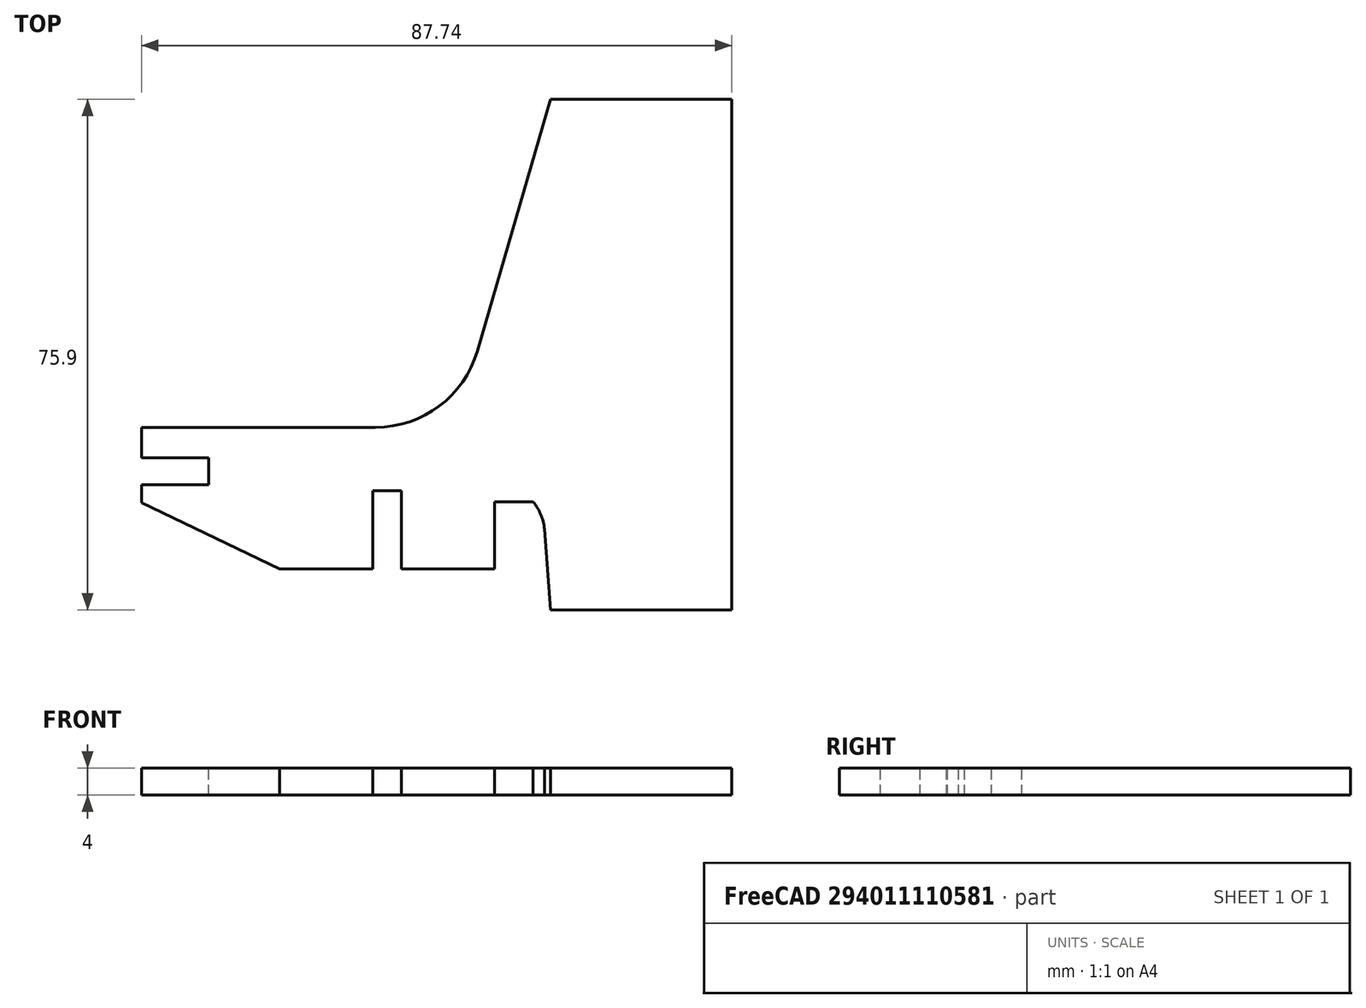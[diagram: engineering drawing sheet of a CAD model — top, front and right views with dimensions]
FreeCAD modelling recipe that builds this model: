
FCSTD DOCUMENT  (FreeCAD 0.18R16131 (Git))
Label: solo_banderuola4mm_v4
License: All rights reserved
LicenseURL: http://en.wikipedia.org/wiki/All_rights_reserved
objects: Sketcher::SketchObject×1, PartDesign::Pad×1, PartDesign::Body×1
note: 4 computed .brp shape members not serialized (recipe doc carries the construction recipe); baked Part::Feature solids carry a one-line shape summary decoded from their .brp

FEATURE [Sketcher::SketchObject] CopySketch004
  sketch-geometry (26):
    g0: LineSegment StartX=-36.5085 StartY=11.06 StartZ=0 EndX=-1.7237 EndY=11.06 EndZ=0
    g1: LineSegment StartX=13.4079 StartY=22.4098 StartZ=0 EndX=24.3191 EndY=59.8325 EndZ=0
    g2: LineSegment StartX=24.3191 StartY=59.8325 StartZ=0 EndX=51.2261 EndY=59.8325 EndZ=0
    g3: ArcOfCircle CenterX=-1.7237 CenterY=26.8216 CenterZ=0 NormalX=0 NormalY=0 NormalZ=1 AngleXU=0 Radius=15.7616 StartAngle=4.71239 EndAngle=5.99948
    g4: GeomPoint X=16 Y=0 Z=0
    g5: LineSegment StartX=-16 StartY=-10 StartZ=0 EndX=-2.15 EndY=-10 EndZ=0
    g6: LineSegment StartX=16 StartY=-10 StartZ=0 EndX=16 EndY=0 EndZ=0
    g7: GeomPoint X=-2.15 Y=-10 Z=0
    g8: GeomPoint X=2.15 Y=-10 Z=0
    g9: LineSegment StartX=-2.15 StartY=-10 StartZ=0 EndX=-2.15 EndY=1.64739 EndZ=0
    g10: LineSegment StartX=-2.15 StartY=1.64739 StartZ=0 EndX=2.15 EndY=1.64739 EndZ=0
    g11: LineSegment StartX=2.15 StartY=1.64739 StartZ=0 EndX=2.15 EndY=-10 EndZ=0
    g12: LineSegment StartX=2.15 StartY=-10 StartZ=0 EndX=16 EndY=-10 EndZ=0
    g13: ArcOfCircle CenterX=15.5785 CenterY=-4.94395 CenterZ=0 NormalX=0 NormalY=0 NormalZ=1 AngleXU=0 Radius=7.87288 StartAngle=0.112427 EndAngle=0.678944
    g14: LineSegment StartX=23.4017 StartY=-4.06069 StartZ=0 EndX=24.3191 EndY=-16.0675 EndZ=0
    g15: LineSegment StartX=24.3191 StartY=-16.0675 StartZ=0 EndX=51.2261 EndY=-16.0675 EndZ=0
    g16: LineSegment StartX=16 StartY=0 StartZ=0 EndX=21.7055 EndY=0 EndZ=0
    g17: LineSegment StartX=-36.5085 StartY=11.06 StartZ=0 EndX=-36.5085 EndY=6.54926 EndZ=0
    g18: LineSegment StartX=-16 StartY=-10 StartZ=0 EndX=-36.5085 EndY=-0.144815 EndZ=0
    g19: LineSegment StartX=-36.5085 StartY=6.54926 StartZ=0 EndX=-26.5085 EndY=6.54926 EndZ=0
    g20: LineSegment StartX=-26.5085 StartY=6.54926 StartZ=0 EndX=-26.5085 EndY=2.54926 EndZ=0
    g21: LineSegment StartX=-26.5085 StartY=2.54926 StartZ=0 EndX=-36.5085 EndY=2.54926 EndZ=0
    g22: LineSegment [constr] StartX=15.9818 StartY=5.77886 StartZ=0 EndX=-16.7629 EndY=5.77886 EndZ=0
    g23: LineSegment [constr] StartX=22.8928 StartY=7.91796 StartZ=0 EndX=-22.1107 EndY=7.91796 EndZ=0
    g24: LineSegment StartX=-36.5085 StartY=2.54926 StartZ=0 EndX=-36.5085 EndY=-0.144815 EndZ=0
    g25: LineSegment StartX=51.2261 StartY=59.8325 StartZ=0 EndX=51.2261 EndY=-16.0675 EndZ=0
  constraints (52):
    c: Horizontal(g0)
    c: Coincident(g1,g2)
    c: Horizontal(g2)
    c: Tangent(g0,g3) = -1.5708
    c: Tangent(g1,g3) = -1.5708
    c: Horizontal(g5)
    c: Coincident(g12,g6)
    c: Vertical(g6)
    c: Coincident(g6,g4)
    c: PointOnObject(g7,g5)
    c: DistanceY(g6,g6) = 10
    c: Symmetric(g7,g8,g-2)
    c: Coincident(g9,g7)
    c: Vertical(g9)
    c: Coincident(g9,g10)
    c: Horizontal(g10)
    c: Coincident(g10,g11)
    c: Coincident(g11,g8)
    c: Vertical(g11)
    c: PointOnObject(g5,g9)
    c: PointOnObject(g12,g11)
    c: Tangent(g5,g12)
    c: DistanceX(g5,g8) = 4.3
    c: Coincident(g14,g15)
    c: Horizontal(g15)
    c: PointOnObject(g4,g-1)
    c: Equal(g2,g15)
    c: Coincident(g16,g4)
    c: Horizontal(g16)
    c: Coincident(g14,g13)
    c: Coincident(g13,g16)
    c: Coincident(g17,g0)
    c: Vertical(g17)
    c: DistanceX(g5,g6) = 32
    c: Coincident(g18,g5)
    c: Coincident(g18,g24)
    c: Coincident(g19,g20)
    c: Coincident(g20,g21)
    c: Horizontal(g19)
    c: Horizontal(g21)
    c: Vertical(g20)
    c: DistanceY(g20,g20) = 4
    c: DistanceX(g21,g21) = 10
    c: Horizontal(g22)
    c: Horizontal(g23)
    c: Coincident(g17,g19)
    c: PointOnObject(g24,g21)
    c: Tangent(g17,g24)
    c: Coincident(g25,g2)
    c: Coincident(g25,g15)
    c: Vertical(g25)
    c: DistanceY(g25,g25) = 75.9
FEATURE [PartDesign::Pad] Pad
  Length = 4
  Length2 = 100
  Midplane = true
  Profile = -> CopySketch004
  Type = 0
FEATURE [PartDesign::Body] Body001
  Group = -> [Pad]
  Origin = -> Origin001
  Tip = -> Pad
